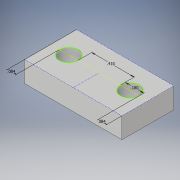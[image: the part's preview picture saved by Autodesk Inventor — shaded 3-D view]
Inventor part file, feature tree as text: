
AUTODESK INVENTOR PART (.ipt)
format: ipt  version: 2019 (Build 230136000, 136)  size: 115,712 bytes
history: native  units: in
note: dims shown in document units (in); Inventor stores cm internally (conversion verified against a paired STEP export)
features: extrude x2, other x2
ambient origin geometry x8: Origin, YZ Plane, XZ Plane, XY Plane, X Axis, Y Axis, Z Axis, Center Point
bodies: Solid1 (feature_tree)
feature tree (4):
  extrude  "Spacer Body"  Depth=0.2in TaperAngle=0.0deg
  extrude  "Spacer Holes"  Depth=0.4in TaperAngle=0.0deg
  other  "Spacer 2D"
  other  "Spacer Circles"
